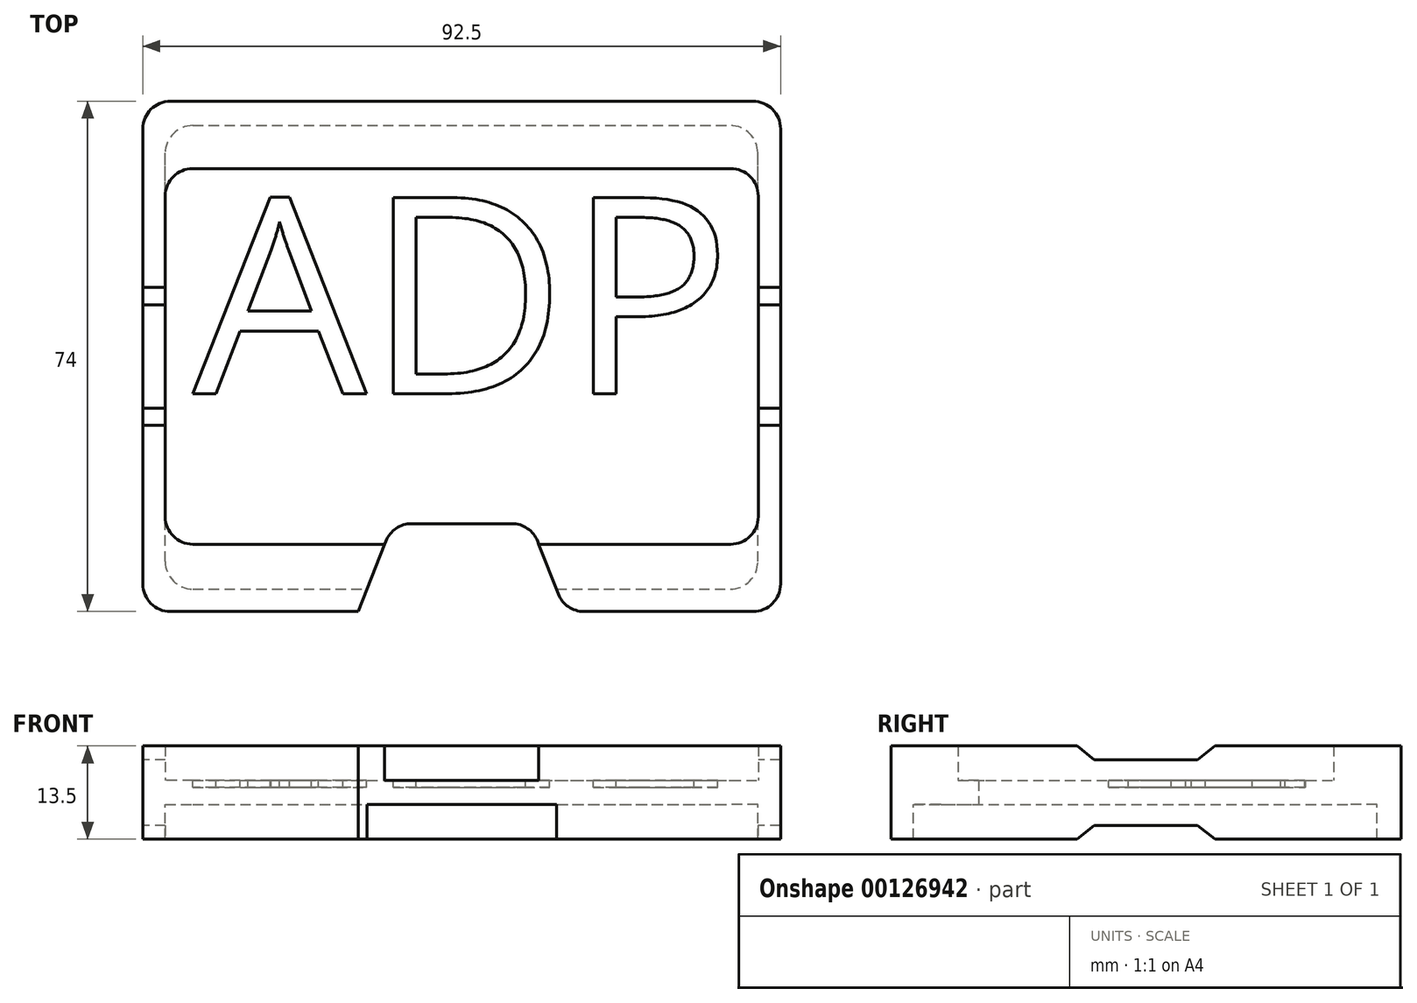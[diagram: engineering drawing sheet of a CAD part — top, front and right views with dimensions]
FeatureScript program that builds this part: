
annotation { "Feature Type Name" : "Feature", "Feature Type Description" : "" }
export const myFeature = defineFeature(function(context is Context, id is Id, definition is map)
    precondition{}
    {
        {
            var Q0;
            Q0=qCreatedBy(makeId("Top.planeOp"),FACE);
            var sketch = newSketch(context, id + "F0", { "sketchPlane" : qUnion([Q0])});
            skLineSegment(sketch, "E0.bottom", {"start": v(4, 0) * mm, "end": v(82, 0) * mm});
            skLineSegment(sketch, "E0.top", {"start": v(4, 54.5) * mm, "end": v(82, 54.5) * mm});
            skLineSegment(sketch, "E0.left", {"start": v(0, 4) * mm, "end": v(0, 50.5) * mm});
            skLineSegment(sketch, "E0.right", {"start": v(86, 4) * mm, "end": v(86, 50.5) * mm});
            skPoint(sketch, "E1.visualSharp", {"position": v(0, 54.5) * mm});
            skArc(sketch, "E1.filletArc", {"start": v(4, 54.5) * mm, "mid": v(1.17, 53.33) * mm, "end": v(0, 50.5) * mm});
            skPoint(sketch, "E2.visualSharp", {"position": v(86, 54.5) * mm});
            skArc(sketch, "E2.filletArc", {"start": v(86, 50.5) * mm, "mid": v(84.83, 53.33) * mm, "end": v(82, 54.5) * mm});
            skPoint(sketch, "E3.visualSharp", {"position": v(86, 0) * mm});
            skArc(sketch, "E3.filletArc", {"start": v(82, 0) * mm, "mid": v(84.83, 1.17) * mm, "end": v(86, 4) * mm});
            skPoint(sketch, "E4.visualSharp", {"position": v(0, 0) * mm});
            skArc(sketch, "E4.filletArc", {"start": v(0, 4) * mm, "mid": v(1.17, 1.17) * mm, "end": v(4, 0) * mm});
            skSolve(sketch);
        }
        {
            var Q0;
            Q0=qCreatedBy(makeId("Top.planeOp"),FACE);
            var sketch = newSketch(context, id + "F1", { "sketchPlane" : qUnion([Q0])});
            skLineSegment(sketch, "E5", {"start": v(0, 0) * mm, "end": v(0, -9.75) * mm, "construction": true});
            skLineSegment(sketch, "E6", {"start": v(0, -9.75) * mm, "end": v(-3.25, -9.75) * mm, "construction": true});
            skLineSegment(sketch, "E7.bottom", {"start": v(0.75, -9.75) * mm, "end": v(85.25, -9.75) * mm});
            skLineSegment(sketch, "E7.top", {"start": v(0.75, 64.25) * mm, "end": v(85.25, 64.25) * mm});
            skLineSegment(sketch, "E7.left", {"start": v(-3.25, -5.75) * mm, "end": v(-3.25, 60.25) * mm});
            skLineSegment(sketch, "E7.right", {"start": v(89.25, -5.75) * mm, "end": v(89.25, 60.25) * mm});
            skPoint(sketch, "E8.0", {"position": v(86, 54.5) * mm});
            skLineSegment(sketch, "E9", {"start": v(86, 54.5) * mm, "end": v(86, 64.25) * mm, "construction": true});
            skLineSegment(sketch, "E10", {"start": v(86, 64.25) * mm, "end": v(89.25, 64.25) * mm, "construction": true});
            skPoint(sketch, "E11.visualSharp", {"position": v(-3.25, 64.25) * mm});
            skArc(sketch, "E11.filletArc", {"start": v(0.75, 64.25) * mm, "mid": v(-2.08, 63.08) * mm, "end": v(-3.25, 60.25) * mm});
            skPoint(sketch, "E12.visualSharp", {"position": v(89.25, 64.25) * mm});
            skArc(sketch, "E12.filletArc", {"start": v(89.25, 60.25) * mm, "mid": v(88.08, 63.08) * mm, "end": v(85.25, 64.25) * mm});
            skPoint(sketch, "E13.visualSharp", {"position": v(89.25, -9.75) * mm});
            skArc(sketch, "E13.filletArc", {"start": v(85.25, -9.75) * mm, "mid": v(88.08, -8.58) * mm, "end": v(89.25, -5.75) * mm});
            skPoint(sketch, "E14.visualSharp", {"position": v(-3.25, -9.75) * mm});
            skArc(sketch, "E14.filletArc", {"start": v(-3.25, -5.75) * mm, "mid": v(-2.08, -8.58) * mm, "end": v(0.75, -9.75) * mm});
            skSolve(sketch);
        }
        {
            var Q0;
            Q0=makeQuery(id+"F1.imprint","IMPRINT",FACE,{"disambiguationData":[TD([[makeQuery(id+"F1.imprint","IMPRINT",EDGE,{"derivedFrom":sQuery(id+"F1.wireOp",EDGE,"E7.bottom")}),1.0]])]});
            extrude(context, id + "F2", {"entities" : qUnion([Q0]), "oppositeDirection" : true, "depth" : 8.5 * mm, "hasSecondDirection" : true, "secondDirectionOppositeDirection" : false, "secondDirectionDepth" : 5 * mm});
        }
        {
            var Q0;
            Q0=makeQuery(id+"F0.imprint","IMPRINT",FACE,{"disambiguationData":[TD([[makeQuery(id+"F0.imprint","IMPRINT",EDGE,{"derivedFrom":sQuery(id+"F0.wireOp",EDGE,"E0.bottom")}),1.0]])]});
            extrude(context, id + "F3", {"entities" : qUnion([Q0]), "operationType" : NewBodyOperationType.REMOVE, "depth" : 5 * mm});
        }
        {
            var Q0;
            Q0=qCreatedBy(makeId("Top.planeOp"),FACE);
            var sketch = newSketch(context, id + "F4", { "sketchPlane" : qUnion([Q0])});
            skLineSegment(sketch, "E15", {"start": v(0, 0) * mm, "end": v(0, -6.5) * mm, "construction": true});
            skLineSegment(sketch, "E16", {"start": v(85.95, 54.24) * mm, "end": v(85.95, 60.74) * mm, "construction": true});
            skLineSegment(sketch, "E17.bottom", {"start": v(4, -6.5) * mm, "end": v(81.95, -6.5) * mm});
            skLineSegment(sketch, "E17.top", {"start": v(4, 60.74) * mm, "end": v(81.95, 60.74) * mm});
            skLineSegment(sketch, "E17.left", {"start": v(0, -2.5) * mm, "end": v(0, 56.74) * mm});
            skLineSegment(sketch, "E17.right", {"start": v(85.95, -2.5) * mm, "end": v(85.95, 56.74) * mm});
            skPoint(sketch, "E18.visualSharp", {"position": v(0, 60.74) * mm});
            skArc(sketch, "E18.filletArc", {"start": v(4, 60.74) * mm, "mid": v(1.17, 59.57) * mm, "end": v(0, 56.74) * mm});
            skPoint(sketch, "E19.visualSharp", {"position": v(85.95, 60.74) * mm});
            skArc(sketch, "E19.filletArc", {"start": v(85.95, 56.74) * mm, "mid": v(84.78, 59.57) * mm, "end": v(81.95, 60.74) * mm});
            skPoint(sketch, "E20.visualSharp", {"position": v(85.95, -6.5) * mm});
            skArc(sketch, "E20.filletArc", {"start": v(81.95, -6.5) * mm, "mid": v(84.78, -5.33) * mm, "end": v(85.95, -2.5) * mm});
            skPoint(sketch, "E21.visualSharp", {"position": v(0, -6.5) * mm});
            skArc(sketch, "E21.filletArc", {"start": v(0, -2.5) * mm, "mid": v(1.17, -5.33) * mm, "end": v(4, -6.5) * mm});
            skSolve(sketch);
        }
        {
            var Q0;
            Q0=makeQuery(id+"F4.imprint","IMPRINT",FACE,{"disambiguationData":[TD([[makeQuery(id+"F4.imprint","IMPRINT",EDGE,{"derivedFrom":sQuery(id+"F4.wireOp",EDGE,"E17.bottom")}),1.0]])]});
            extrude(context, id + "F5", {"entities" : qUnion([Q0]), "operationType" : NewBodyOperationType.REMOVE, "oppositeDirection" : true, "depth" : 8.5 * mm, "hasSecondDirection" : true, "secondDirectionOppositeDirection" : true, "secondDirectionDepth" : 3.5 * mm});
        }
        {
            var Q0;
            Q0=qCreatedBy(makeId("Top.planeOp"),FACE);
            var sketch = newSketch(context, id + "F6", { "sketchPlane" : qUnion([Q0])});
            skLineSegment(sketch, "E22.0", {"start": v(0.75, -9.75) * mm, "end": v(85.25, -9.75) * mm});
            skLineSegment(sketch, "E23", {"start": v(43, -9.75) * mm, "end": v(43, 3) * mm, "construction": true});
            skLineSegment(sketch, "E24", {"start": v(43, 3) * mm, "end": v(50.27, 3) * mm});
            skLineSegment(sketch, "E25", {"start": v(43, -9.75) * mm, "end": v(58, -9.75) * mm});
            skLineSegment(sketch, "E26", {"start": v(54, 0.46) * mm, "end": v(58, -9.75) * mm});
            skLineSegment(sketch, "E27.MirrorCS", {"start": v(43, -9.75) * mm, "end": v(28, -9.75) * mm});
            skLineSegment(sketch, "E28.MirrorCS", {"start": v(43, 3) * mm, "end": v(35.73, 3) * mm});
            skLineSegment(sketch, "E29.MirrorCS", {"start": v(32, 0.46) * mm, "end": v(28, -9.75) * mm});
            skPoint(sketch, "E30.visualSharp", {"position": v(33, 3) * mm});
            skArc(sketch, "E30.filletArc", {"start": v(35.73, 3) * mm, "mid": v(33.47, 2.3) * mm, "end": v(32, 0.46) * mm});
            skPoint(sketch, "E31.visualSharp", {"position": v(53, 3) * mm});
            skArc(sketch, "E31.filletArc", {"start": v(54, 0.46) * mm, "mid": v(52.53, 2.3) * mm, "end": v(50.27, 3) * mm});
            skSolve(sketch);
        }
        {
            var Q0;
            Q0=makeQuery(id+"F6.imprint","IMPRINT",FACE,{"disambiguationData":[TD([[makeQuery(id+"F6.imprint","IMPRINT",EDGE,{"derivedFrom":sQuery(id+"F6.wireOp",EDGE,"E24")}),-1.0]])]});
            extrude(context, id + "F7", {"entities" : qUnion([Q0]), "operationType" : NewBodyOperationType.REMOVE, "depth" : 5 * mm, "hasSecondDirection" : true, "secondDirectionOppositeDirection" : true, "secondDirectionDepth" : 8.5 * mm});
        }
        {
            var Q0;
            Q0=makeQuery(id+"F7.boolean.opBoolean","COPY",EDGE,{"derivedFrom":makeQuery(id+"F7.opExtrude","SWEPT_EDGE",EDGE,{"disambiguationData":[OSD([sQuery(id+"F6.wireOp",EDGE,"E25"),sQuery(id+"F6.wireOp",EDGE,"E26")])]})});
            var Q1;
            Q1=makeQuery(id+"F7.boolean.opBoolean","COPY",EDGE,{"derivedFrom":makeQuery(id+"F7.opExtrude","SWEPT_EDGE",EDGE,{"disambiguationData":[OSD([sQuery(id+"F6.wireOp",EDGE,"E27.MirrorCS"),sQuery(id+"F6.wireOp",EDGE,"E29.MirrorCS")])]})});
            fillet(context, id + "F8", {"entities" : qUnion([Q0, Q1]), "radius" : 4 * mm, "tangentPropagation" : true, "allowEdgeOverflow" : false});
        }
        {
            var Q0;
            Q0=makeQuery(id+"F3.boolean.opBoolean","COPY",FACE,{"derivedFrom":makeQuery(id+"F3.opExtrude","CAP_FACE",FACE,{"disambiguationData":[OSD([sQuery(id+"F0.wireOp",EDGE,"E0.bottom"),sQuery(id+"F0.wireOp",EDGE,"E0.top"),sQuery(id+"F0.wireOp",EDGE,"E0.left"),sQuery(id+"F0.wireOp",EDGE,"E0.right"),sQuery(id+"F0.wireOp",EDGE,"E1.filletArc"),sQuery(id+"F0.wireOp",EDGE,"E2.filletArc"),sQuery(id+"F0.wireOp",EDGE,"E3.filletArc"),sQuery(id+"F0.wireOp",EDGE,"E4.filletArc")])],"isStart":true})});
            var sketch = newSketch(context, id + "F9", { "sketchPlane" : qUnion([Q0])});
            skText(sketch, "E32", { "text": "ADP", "fontName": "OpenSans-Regular.ttf"});
            const initialGuessF9  = {"E32": [0.004, 0.02185, 1, 0, 0.02865]};
            skSetInitialGuess(sketch, initialGuessF9);
            skSolve(sketch);
        }
        {
            var Q0;
            Q0=qSketchRegion(id+"F9",true);
            var Q1;
            Q1=makeQuery(id+"F9.imprint","IMPRINT",FACE,{"disambiguationData":[TD([[makeQuery(id+"F9.imprint","IMPRINT",EDGE,{"derivedFrom":sQuery(id+"F9.wireOp",EDGE,"E32.sketch_text.stroke-0")}),-1.0]])]});
            extrude(context, id + "F10", {"entities" : qUnion([Q0, Q1]), "operationType" : NewBodyOperationType.REMOVE, "oppositeDirection" : true, "depth" : 1 * mm});
        }
        {
            var Q0;
            Q0=makeQuery(id+"F2.opExtrude","SWEPT_FACE",FACE,{"disambiguationData":[OSD([sQuery(id+"F1.wireOp",EDGE,"E7.left")])]});
            var sketch = newSketch(context, id + "F11", { "sketchPlane" : qUnion([Q0])});
            skLineSegment(sketch, "E33.0", {"start": v(5.75, 5) * mm, "end": v(-60.25, 5) * mm});
            skLineSegment(sketch, "E34", {"start": v(-27.25, 5) * mm, "end": v(-27.25, 3) * mm, "construction": true});
            skLineSegment(sketch, "E35", {"start": v(-27.25, 3) * mm, "end": v(-19.75, 3) * mm});
            skLineSegment(sketch, "E36", {"start": v(-27.25, 5) * mm, "end": v(-17.25, 5) * mm});
            skLineSegment(sketch, "E37", {"start": v(-17.25, 5) * mm, "end": v(-19.75, 3) * mm});
            skLineSegment(sketch, "E38.MirrorCS", {"start": v(-27.25, 5) * mm, "end": v(-37.25, 5) * mm});
            skLineSegment(sketch, "E39.MirrorCS", {"start": v(-37.25, 5) * mm, "end": v(-34.75, 3) * mm});
            skLineSegment(sketch, "E40.MirrorCS", {"start": v(-27.25, 3) * mm, "end": v(-34.75, 3) * mm});
            skLineSegment(sketch, "E41.0", {"start": v(5.75, -8.5) * mm, "end": v(5.75, 5) * mm});
            skLineSegment(sketch, "E42", {"start": v(5.75, -1.75) * mm, "end": v(-44.25, -1.75) * mm, "construction": true});
            skLineSegment(sketch, "E43.MirrorCS", {"start": v(-27.25, -8.5) * mm, "end": v(-37.25, -8.5) * mm});
            skLineSegment(sketch, "E44.MirrorCS", {"start": v(-17.25, -8.5) * mm, "end": v(-19.75, -6.5) * mm});
            skLineSegment(sketch, "E45.MirrorCS", {"start": v(-27.25, -8.5) * mm, "end": v(-17.25, -8.5) * mm});
            skLineSegment(sketch, "E46.MirrorCS", {"start": v(-27.25, -6.5) * mm, "end": v(-19.75, -6.5) * mm});
            skLineSegment(sketch, "E47.MirrorCS", {"start": v(-27.25, -6.5) * mm, "end": v(-34.75, -6.5) * mm});
            skLineSegment(sketch, "E48.MirrorCS", {"start": v(-37.25, -8.5) * mm, "end": v(-34.75, -6.5) * mm});
            skSolve(sketch);
        }
        {
            var Q0;
            Q0=makeQuery(id+"F11.imprint","IMPRINT",FACE,{"disambiguationData":[TD([[makeQuery(id+"F11.imprint","IMPRINT",EDGE,{"derivedFrom":sQuery(id+"F11.wireOp",EDGE,"E35")}),1.0]])]});
            var Q1;
            Q1=makeQuery(id+"F11.imprint","IMPRINT",FACE,{"disambiguationData":[TD([[makeQuery(id+"F11.imprint","IMPRINT",EDGE,{"derivedFrom":sQuery(id+"F11.wireOp",EDGE,"E43.MirrorCS")}),-1.0]])]});
            extrude(context, id + "F12", {"entities" : qUnion([Q0, Q1]), "operationType" : NewBodyOperationType.REMOVE, "endBound" : BoundingType.THROUGH_ALL, "oppositeDirection" : true, "depth" : 25 * mm});
        }
    });
